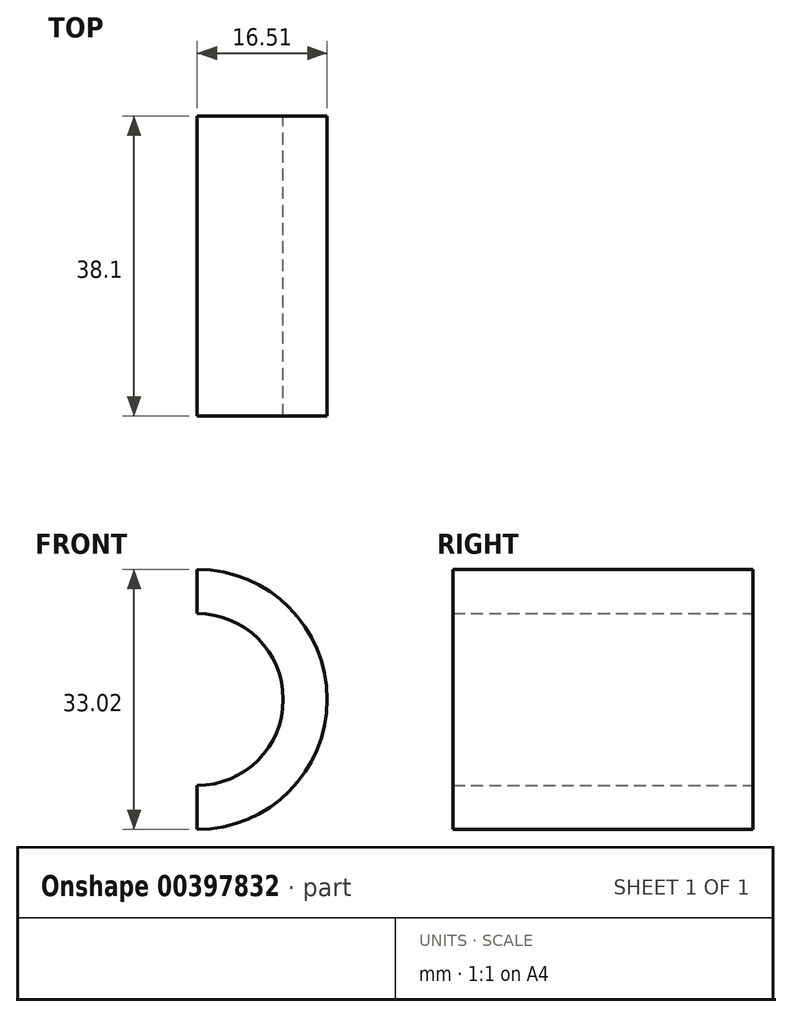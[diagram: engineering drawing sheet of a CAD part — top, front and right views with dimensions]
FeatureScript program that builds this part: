
annotation { "Feature Type Name" : "Feature", "Feature Type Description" : "" }
export const myFeature = defineFeature(function(context is Context, id is Id, definition is map)
    precondition{}
    {
        {
            var Q0;
            Q0=qCreatedBy(makeId("Front.planeOp"),FACE);
            var sketch = newSketch(context, id + "F0", { "sketchPlane" : qUnion([Q0])});
            skPoint(sketch, "E0.middle", {"position": v(0, 0) * mm});
            skArc(sketch, "E1", {"start": v(32.61, -16.51) * mm, "mid": v(49.12, 0) * mm, "end": v(32.61, 16.51) * mm});
            skArc(sketch, "E2.0", {"start": v(32.61, -10.92) * mm, "mid": v(43.53, 0) * mm, "end": v(32.61, 10.92) * mm});
            skLineSegment(sketch, "E3", {"start": v(32.61, 16.51) * mm, "end": v(32.61, 10.92) * mm});
            skLineSegment(sketch, "E4", {"start": v(32.61, -10.92) * mm, "end": v(32.61, -16.51) * mm});
            skSolve(sketch);
        }
        {
            var Q0;
            Q0=makeQuery(id+"F0.imprint","IMPRINT",FACE,{"disambiguationData":[TD([[makeQuery(id+"F0.imprint","IMPRINT",EDGE,{"derivedFrom":sQuery(id+"F0.wireOp",EDGE,"E1")}),1.0]])]});
            extrude(context, id + "F1", {"entities" : qUnion([Q0]), "depth" : 38.1 * mm});
        }
    });
